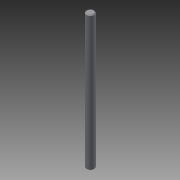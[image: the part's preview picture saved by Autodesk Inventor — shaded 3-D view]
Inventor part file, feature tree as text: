
AUTODESK INVENTOR PART (.ipt)
format: ipt  version: 2015 (Build 190159000, 159)  size: 81,920 bytes
history: native  units: in
note: dims shown in document units (in); Inventor stores cm internally (conversion verified against a paired STEP export)
features: other x3, extrude x1, chamfer x1, sketch x1
ambient origin geometry x8: Origin, YZ Plane, XZ Plane, XY Plane, X Axis, Y Axis, Z Axis, Center Point
bodies: Solid1 (feature_tree)
feature tree (6):
  other  "Axle-100mm - 739088.ipt"
  extrude  "Extrusion1"  Depth=0.3937in TaperAngle=0.0deg
  chamfer  "Chamfer1"  Distance=0.0197in Angle=45.0deg
  other  "tetrix_739088_2013::Axle-100mm - 739088.ipt"
  other  "TaggingFeature1"
  sketch  "Sketch1"  dims[d0=0.3937in d1=0.75in d2=0.0in d3=0.0197in d4=0.125in d5=45.0deg]
